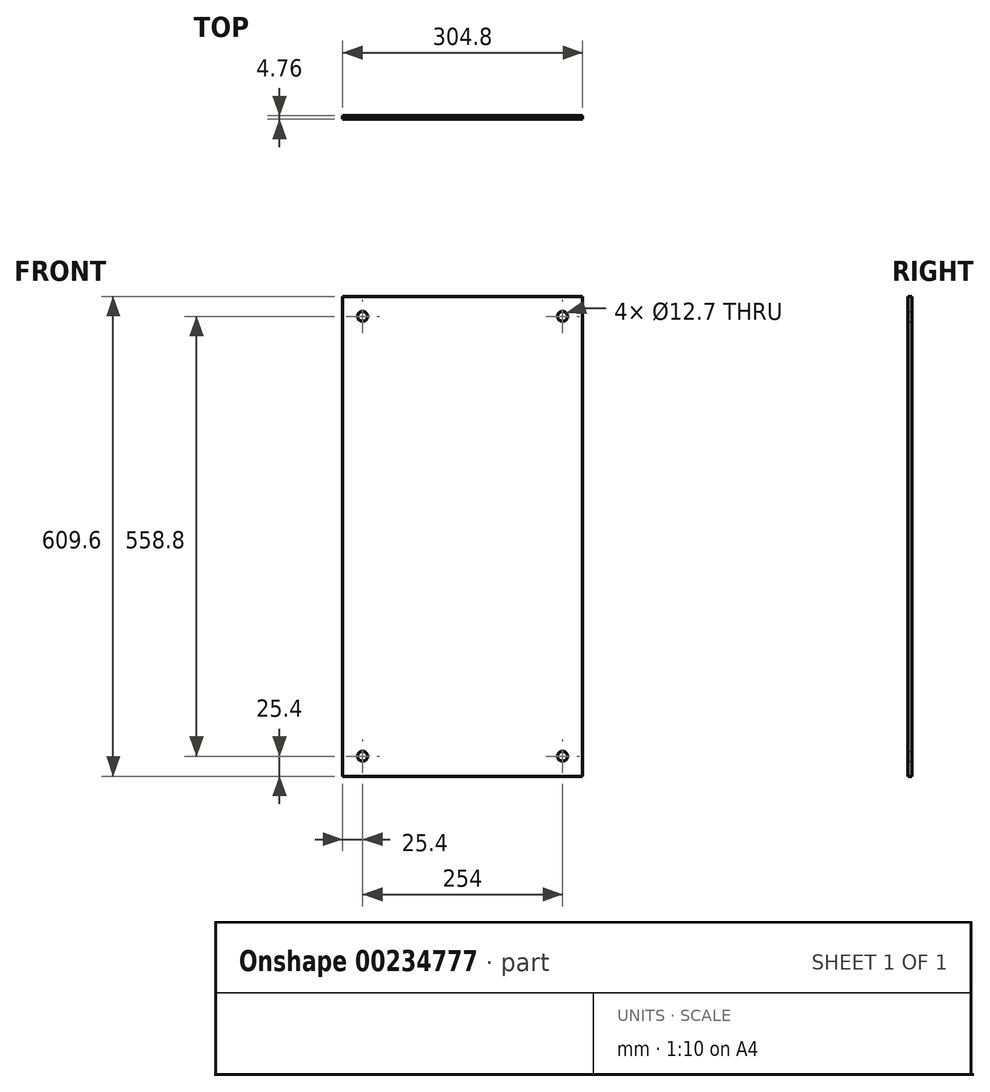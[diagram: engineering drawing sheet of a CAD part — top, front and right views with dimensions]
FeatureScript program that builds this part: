
annotation { "Feature Type Name" : "Feature", "Feature Type Description" : "" }
export const myFeature = defineFeature(function(context is Context, id is Id, definition is map)
    precondition{}
    {
        {
            var Q0;
            Q0=qCreatedBy(makeId("Front.planeOp"),FACE);
            var sketch = newSketch(context, id + "F0", { "sketchPlane" : qUnion([Q0])});
            skLineSegment(sketch, "E0.bottom", {"start": v(152.4, -304.8) * mm, "end": v(-152.4, -304.8) * mm});
            skLineSegment(sketch, "E0.top", {"start": v(152.4, 304.8) * mm, "end": v(-152.4, 304.8) * mm});
            skLineSegment(sketch, "E0.left", {"start": v(152.4, -304.8) * mm, "end": v(152.4, 304.8) * mm});
            skLineSegment(sketch, "E0.right", {"start": v(-152.4, -304.8) * mm, "end": v(-152.4, 304.8) * mm});
            skPoint(sketch, "E0.middle", {"position": v(0, 0) * mm});
            skPoint(sketch, "E1", {"position": v(-127, 279.4) * mm});
            skPoint(sketch, "E2", {"position": v(127, 279.4) * mm});
            skPoint(sketch, "E3", {"position": v(127, -279.4) * mm});
            skPoint(sketch, "E4", {"position": v(-127, -279.4) * mm});
            skSolve(sketch);
        }
        {
            var Q0;
            Q0=makeQuery(id+"F0.imprint","IMPRINT",FACE,{"disambiguationData":[TD([[makeQuery(id+"F0.imprint","IMPRINT",EDGE,{"derivedFrom":sQuery(id+"F0.wireOp",EDGE,"E0.bottom")}),-1.0]])]});
            extrude(context, id + "F2", {"entities" : qUnion([Q0]), "depth" : 4.76 * mm});
        }
        {
            var Q0;
            Q0=sQuery(id+"F0.wireOp",VERTEX,"E1");
            var Q1;
            Q1=sQuery(id+"F0.wireOp",VERTEX,"E2");
            var Q2;
            Q2=sQuery(id+"F0.wireOp",VERTEX,"E4");
            var Q3;
            Q3=sQuery(id+"F0.wireOp",VERTEX,"E3");
            var Q4;
            Q4=makeQuery(id+"F2.opExtrude","SWEPT_BODY",BODY,{"disambiguationData":[OSD([sQuery(id+"F0.wireOp",EDGE,"E0.bottom"),sQuery(id+"F0.wireOp",EDGE,"E0.top"),sQuery(id+"F0.wireOp",EDGE,"E0.left"),sQuery(id+"F0.wireOp",EDGE,"E0.right")])]});
            hole(context, id + "F1", {"style" : HoleStyle.SIMPLE, "endStyle" : HoleEndStyle.THROUGH, "oppositeDirection" : true, "holeDiameter" : 12.7 * mm, "locations" : qUnion([Q0, Q1, Q2, Q3]), "scope" : qUnion([Q4]), "isTappedThrough" : true});
        }
    });
